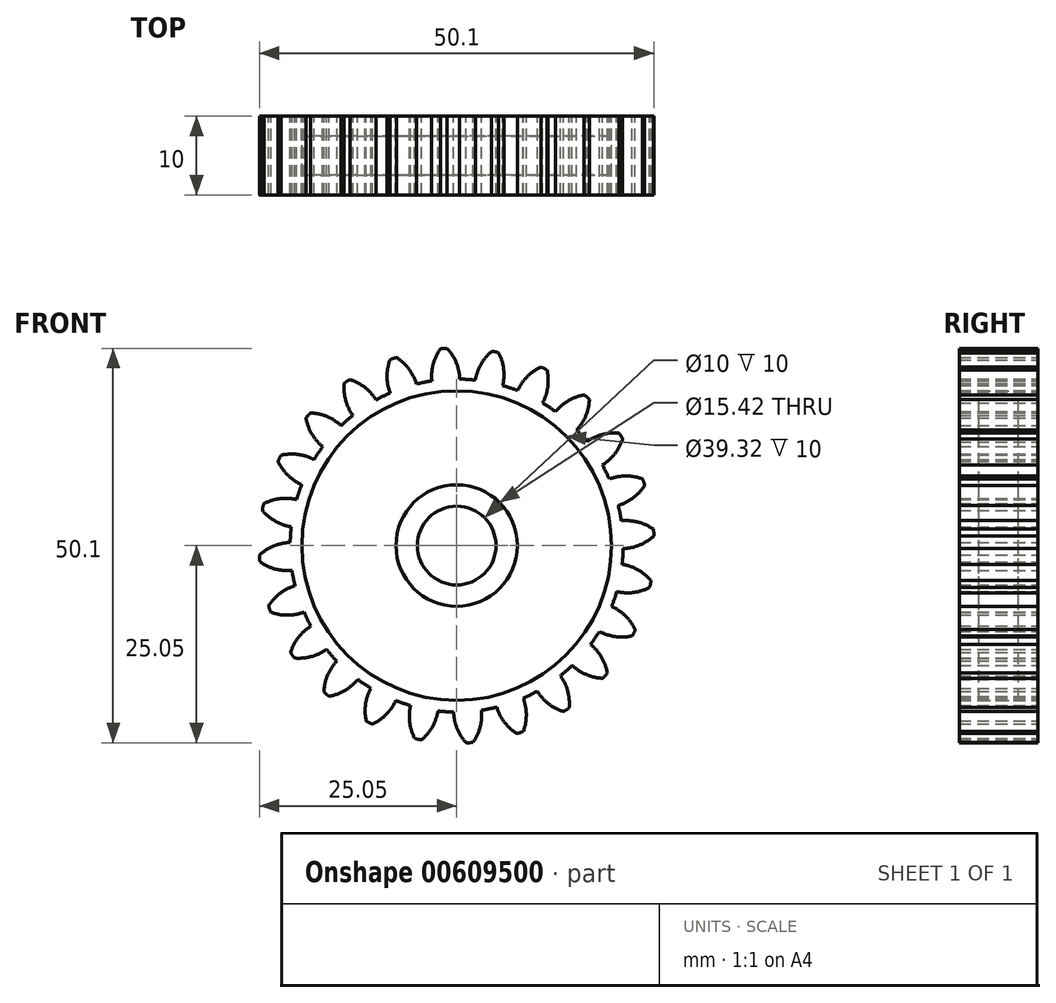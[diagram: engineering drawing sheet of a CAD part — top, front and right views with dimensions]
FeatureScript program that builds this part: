
annotation { "Feature Type Name" : "Feature", "Feature Type Description" : "" }
export const myFeature = defineFeature(function(context is Context, id is Id, definition is map)
    precondition{}
    {
        {
            var Q0;
            Q0=qCreatedBy(makeId("Front.planeOp"),FACE);
            var sketch = newSketch(context, id + "F0", { "sketchPlane" : qUnion([Q0])});
            skCircle(sketch, "E0", {"center": v(0, 0) * mm, "radius": 21.15 * mm});
            skCircle(sketch, "E1", {"center": v(0, 0) * mm, "radius": 23.1 * mm, "construction": true});
            skCircle(sketch, "E2", {"center": v(0, 0) * mm, "radius": 25 * mm, "construction": true});
            skLineSegment(sketch, "E3", {"start": v(0, 0) * mm, "end": v(0, 38.41) * mm, "construction": true});
            skLineSegment(sketch, "E4", {"start": v(0, 0) * mm, "end": v(-2.5, 38.12) * mm, "construction": true});
            skLineSegment(sketch, "E5", {"start": v(0, 23.1) * mm, "end": v(-24.7, 14.1) * mm, "construction": true});
            skLineSegment(sketch, "E6", {"start": v(0, 23.1) * mm, "end": v(-23.8, 23.1) * mm, "construction": true});
            skCircle(sketch, "E7", {"center": v(0, 23.1) * mm, "radius": 5.75 * mm, "construction": true});
            skCircle(sketch, "E8", {"center": v(0, 0) * mm, "radius": 21.7 * mm, "construction": true});
            skArc(sketch, "E9", {"start": v(0, 23.1) * mm, "mid": v(-0.5, 24.12) * mm, "end": v(-1.2, 25.03) * mm});
            skArc(sketch, "E10", {"start": v(0.39, 21.13) * mm, "mid": v(0.28, 22.13) * mm, "end": v(0, 23.1) * mm});
            skArc(sketch, "E11.MirrorCS", {"start": v(-3.02, 22.9) * mm, "mid": v(-2.65, 23.98) * mm, "end": v(-2.08, 24.98) * mm});
            skArc(sketch, "E12.MirrorCS", {"start": v(-3.14, 20.9) * mm, "mid": v(-3.16, 21.9) * mm, "end": v(-3.02, 22.9) * mm});
            skArc(sketch, "E13", {"start": v(-1.2, 25.03) * mm, "mid": v(-1.64, 25.05) * mm, "end": v(-2.08, 24.98) * mm});
            skCircle(sketch, "E14", {"center": v(0, 0) * mm, "radius": 5 * mm});
            skCircle(sketch, "E15", {"center": v(0, 0) * mm, "radius": 19.66 * mm});
            skCircle(sketch, "E16", {"center": v(0, 0) * mm, "radius": 7.7 * mm});
            skSolve(sketch);
        }
        {
            var Q0;
            {var subQ0=sQuery(id+"F0.wireOp",EDGE,"E0");var subQ1=makeQuery(id+"F0.imprint","INTERSECT",VERTEX,{"derivedFrom":[subQ0,sQuery(id+"F0.wireOp",EDGE,"E10")]});Q0=makeQuery(id+"F0.imprint","IMPRINT",FACE,{"disambiguationData":[TD([[makeQuery(id+"F0.imprint","IMPRINT",EDGE,{"disambiguationData":[TD([[subQ1,-1.0]])],"derivedFrom":subQ0}),1.0]])]});}
            var Q1;
            {var subQ2=sQuery(id+"F0.wireOp",EDGE,"E9");Q1=makeQuery(id+"F0.imprint","IMPRINT",FACE,{"disambiguationData":[TD([[makeQuery(id+"F0.imprint","IMPRINT",EDGE,{"derivedFrom":subQ2}),1.0]])]});}
            extrude(context, id + "F1", {"entities" : qUnion([Q0, Q1]), "endBound" : BoundingType.SYMMETRIC, "depth" : 10 * mm, "offsetDistance" : 25 * mm});
        }
        {
            var Q0;
            Q0=makeQuery(id+"F1.opExtrude","SWEPT_BODY",BODY,{"disambiguationData":[OSD([sQuery(id+"F0.wireOp",EDGE,"E0"),sQuery(id+"F0.wireOp",EDGE,"E9"),sQuery(id+"F0.wireOp",EDGE,"E10"),sQuery(id+"F0.wireOp",EDGE,"E11.MirrorCS"),sQuery(id+"F0.wireOp",EDGE,"E12.MirrorCS"),sQuery(id+"F0.wireOp",EDGE,"E13")])]});
            var Q1;
            Q1=makeQuery(id+"F1.opExtrude","SWEPT_FACE",FACE,{"disambiguationData":[OSD([sQuery(id+"F0.wireOp",EDGE,"E0")])]});
            circularPattern(context, id + "F2", {"entities" : qUnion([Q0]), "axis" : qUnion([Q1]), "angle" : 360 * degree, "instanceCount" : 24, "equalSpace" : true, "isCentered" : true});
        }
        {
            var Q0;
            Q0 = qSketchRegion(id + "F0", true);
            var Q1;
            Q1=makeQuery(id+"F0.imprint","IMPRINT",FACE,{"disambiguationData":[TD([[makeQuery(id+"F0.imprint","IMPRINT",EDGE,{"derivedFrom":sQuery(id+"F0.wireOp",EDGE,"E14")}),-1.0]])]});
            extrude(context, id + "F3", {"entities" : qUnion([Q0, Q1]), "operationType" : NewBodyOperationType.ADD, "endBound" : BoundingType.SYMMETRIC, "depth" : 10 * mm, "offsetDistance" : 25 * mm});
        }
        {
            var Q0;
            Q0=makeQuery(id+"F0.imprint","IMPRINT",FACE,{"disambiguationData":[TD([[makeQuery(id+"F0.imprint","IMPRINT",EDGE,{"derivedFrom":sQuery(id+"F0.wireOp",EDGE,"E15")}),1.0]])]});
            extrude(context, id + "F4", {"entities" : qUnion([Q0]), "endBound" : BoundingType.SYMMETRIC, "depth" : 5 * mm, "offsetDistance" : 25 * mm});
        }
    });
